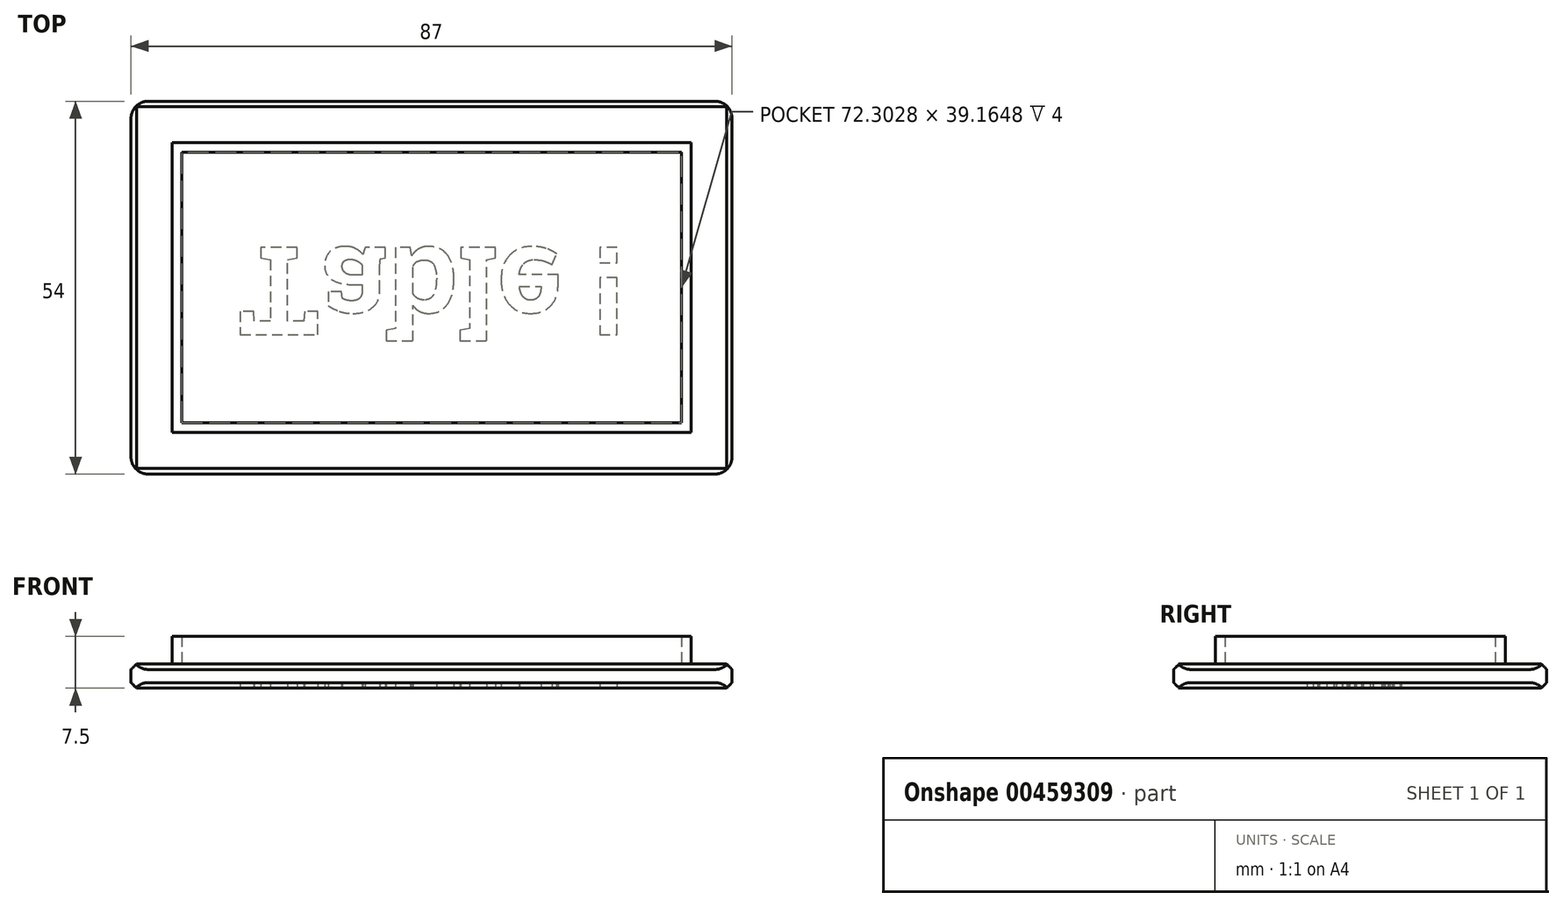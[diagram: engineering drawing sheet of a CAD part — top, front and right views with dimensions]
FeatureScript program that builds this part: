
annotation { "Feature Type Name" : "Feature", "Feature Type Description" : "" }
export const myFeature = defineFeature(function(context is Context, id is Id, definition is map)
    precondition{}
    {
        {
            var Q0;
            Q0=qCreatedBy(makeId("Top.planeOp"),FACE);
            var sketch = newSketch(context, id + "F0", { "sketchPlane" : qUnion([Q0])});
            skLineSegment(sketch, "E0.bottom", {"start": v(43.5, 27) * mm, "end": v(-43.5, 27) * mm});
            skLineSegment(sketch, "E0.top", {"start": v(43.5, -27) * mm, "end": v(-43.5, -27) * mm});
            skLineSegment(sketch, "E0.left", {"start": v(43.5, 27) * mm, "end": v(43.5, -27) * mm});
            skLineSegment(sketch, "E0.right", {"start": v(-43.5, 27) * mm, "end": v(-43.5, -27) * mm});
            skPoint(sketch, "E0.middle", {"position": v(0, 0) * mm});
            skSolve(sketch);
        }
        {
            var Q0;
            Q0 = qSketchRegion(id + "F0", true);
            extrude(context, id + "F1", {"entities" : qUnion([Q0]), "oppositeDirection" : true, "depth" : 3.5 * mm});
        }
        {
            var Q0;
            Q0=makeQuery(id+"F1.opExtrude","CAP_EDGE",EDGE,{"disambiguationData":[OSD([sQuery(id+"F0.wireOp",EDGE,"E0.top")])],"isStart":false});
            var Q1;
            Q1=makeQuery(id+"F1.opExtrude","CAP_EDGE",EDGE,{"disambiguationData":[OSD([sQuery(id+"F0.wireOp",EDGE,"E0.right")])],"isStart":false});
            var Q2;
            Q2=makeQuery(id+"F1.opExtrude","CAP_EDGE",EDGE,{"disambiguationData":[OSD([sQuery(id+"F0.wireOp",EDGE,"E0.bottom")])],"isStart":false});
            var Q3;
            Q3=makeQuery(id+"F1.opExtrude","CAP_EDGE",EDGE,{"disambiguationData":[OSD([sQuery(id+"F0.wireOp",EDGE,"E0.left")])],"isStart":false});
            var Q4;
            Q4=makeQuery(id+"F1.opExtrude","CAP_EDGE",EDGE,{"disambiguationData":[OSD([sQuery(id+"F0.wireOp",EDGE,"E0.top")])],"isStart":true});
            var Q5;
            Q5=makeQuery(id+"F1.opExtrude","CAP_EDGE",EDGE,{"disambiguationData":[OSD([sQuery(id+"F0.wireOp",EDGE,"E0.right")])],"isStart":true});
            var Q6;
            Q6=makeQuery(id+"F1.opExtrude","CAP_EDGE",EDGE,{"disambiguationData":[OSD([sQuery(id+"F0.wireOp",EDGE,"E0.left")])],"isStart":true});
            var Q7;
            Q7=makeQuery(id+"F1.opExtrude","CAP_EDGE",EDGE,{"disambiguationData":[OSD([sQuery(id+"F0.wireOp",EDGE,"E0.bottom")])],"isStart":true});
            chamfer(context, id + "F2", {"entities" : qUnion([Q0, Q1, Q2, Q3, Q4, Q5, Q6, Q7]), "width" : 0.8 * mm, "tangentPropagation" : true});
        }
        {
            var Q0;
            Q0=makeQuery(id+"F1.opExtrude","SWEPT_EDGE",EDGE,{"disambiguationData":[OSD([sQuery(id+"F0.wireOp",EDGE,"E0.top"),sQuery(id+"F0.wireOp",EDGE,"E0.right")])]});
            var Q1;
            Q1=makeQuery(id+"F1.opExtrude","SWEPT_EDGE",EDGE,{"disambiguationData":[OSD([sQuery(id+"F0.wireOp",EDGE,"E0.bottom"),sQuery(id+"F0.wireOp",EDGE,"E0.right")])]});
            var Q2;
            Q2=makeQuery(id+"F1.opExtrude","SWEPT_EDGE",EDGE,{"disambiguationData":[OSD([sQuery(id+"F0.wireOp",EDGE,"E0.bottom"),sQuery(id+"F0.wireOp",EDGE,"E0.left")])]});
            var Q3;
            Q3=makeQuery(id+"F1.opExtrude","SWEPT_EDGE",EDGE,{"disambiguationData":[OSD([sQuery(id+"F0.wireOp",EDGE,"E0.top"),sQuery(id+"F0.wireOp",EDGE,"E0.left")])]});
            fillet(context, id + "F3", {"entities" : qUnion([Q0, Q1, Q2, Q3]), "radius" : 2.5 * mm, "tangentPropagation" : true, "allowEdgeOverflow" : false});
        }
        {
            var Q0;
            Q0=makeQuery(id+"F0.imprint","IMPRINT",FACE,{"disambiguationData":[TD([[makeQuery(id+"F0.imprint","IMPRINT",EDGE,{"derivedFrom":sQuery(id+"F0.wireOp",EDGE,"E0.bottom")}),1.0]])]});
            var sketch = newSketch(context, id + "F4", { "sketchPlane" : qUnion([Q0])});
            skLineSegment(sketch, "E1.bottom", {"start": v(37.55, 20.98) * mm, "end": v(-37.55, 20.98) * mm});
            skLineSegment(sketch, "E1.top", {"start": v(37.55, -20.98) * mm, "end": v(-37.55, -20.98) * mm});
            skLineSegment(sketch, "E1.left", {"start": v(37.55, 20.98) * mm, "end": v(37.55, -20.98) * mm});
            skLineSegment(sketch, "E1.right", {"start": v(-37.55, 20.98) * mm, "end": v(-37.55, -20.98) * mm});
            skPoint(sketch, "E1.middle", {"position": v(0, 0) * mm});
            skLineSegment(sketch, "E2.0", {"start": v(36.15, -19.58) * mm, "end": v(-36.15, -19.58) * mm});
            skLineSegment(sketch, "E2.1", {"start": v(36.15, 19.58) * mm, "end": v(36.15, -19.58) * mm});
            skLineSegment(sketch, "E2.2", {"start": v(36.15, 19.58) * mm, "end": v(-36.15, 19.58) * mm});
            skLineSegment(sketch, "E2.3", {"start": v(-36.15, 19.58) * mm, "end": v(-36.15, -19.58) * mm});
            skSolve(sketch);
        }
        {
            var Q0;
            Q0 = qSketchRegion(id + "F4", true);
            extrude(context, id + "F5", {"entities" : qUnion([Q0]), "operationType" : NewBodyOperationType.ADD, "depth" : 4 * mm});
        }
        {
            var Q0;
            Q0=makeQuery(id+"F4.imprint","IMPRINT",FACE,{"disambiguationData":[TD([[makeQuery(id+"F4.imprint","IMPRINT",EDGE,{"derivedFrom":sQuery(id+"F4.wireOp",EDGE,"E1.bottom")}),-1.0]])]});
            var sketch = newSketch(context, id + "F6", { "sketchPlane" : qUnion([Q0])});
            skCircle(sketch, "E3", {"center": v(-36.85, 20.28) * mm, "radius": 2.2 * mm});
            skLineSegment(sketch, "E4", {"start": v(37.55, 20.98) * mm, "end": v(36.15, 19.58) * mm});
            skLineSegment(sketch, "E5", {"start": v(36.15, -19.58) * mm, "end": v(37.55, -20.98) * mm});
            skLineSegment(sketch, "E6", {"start": v(-36.15, -19.58) * mm, "end": v(-37.55, -20.98) * mm});
            skCircle(sketch, "E7.0.1.0", {"center": v(-36.85, -20.28) * mm, "radius": 2.2 * mm});
            skCircle(sketch, "E7.1.0.0", {"center": v(36.85, 20.28) * mm, "radius": 2.2 * mm});
            skCircle(sketch, "E7.1.1.0", {"center": v(36.85, -20.28) * mm, "radius": 2.2 * mm});
            skLineSegment(sketch, "E7.direction1", {"start": v(-36.85, 20.28) * mm, "end": v(36.85, 20.28) * mm, "construction": true});
            skLineSegment(sketch, "E7.direction2", {"start": v(-36.85, 20.28) * mm, "end": v(-36.85, -20.28) * mm, "construction": true});
            skSolve(sketch);
        }
        {
            var Q0;
            Q0=sQuery(id+"F6.wireOp",EDGE,"E3");
            var Q1;
            Q1=sQuery(id+"F6.wireOp",EDGE,"E7.0.1.0");
            var Q2;
            Q2=sQuery(id+"F6.wireOp",EDGE,"E7.1.1.0");
            var Q3;
            Q3=sQuery(id+"F6.wireOp",EDGE,"E7.1.0.0");
            extrude(context, id + "F7", {"bodyType" : ToolBodyType.SURFACE, "surfaceEntities" : qUnion([Q0, Q1, Q2, Q3]), "depth" : 38 * mm});
        }
        {
            var Q0;
            Q0=makeQuery(id+"F1.opExtrude","CAP_FACE",FACE,{"disambiguationData":[OSD([sQuery(id+"F0.wireOp",EDGE,"E0.bottom"),sQuery(id+"F0.wireOp",EDGE,"E0.top"),sQuery(id+"F0.wireOp",EDGE,"E0.left"),sQuery(id+"F0.wireOp",EDGE,"E0.right")])],"isStart":false});
            var sketch = newSketch(context, id + "F8", { "sketchPlane" : qUnion([Q0])});
            skText(sketch, "E8", { "text": "Table !", "fontName": "RobotoSlab-Bold.ttf"});
            const initialGuessF8  = {"E8": [-0.02804, -0.0058, 1, 0, 0.01277]};
            skSetInitialGuess(sketch, initialGuessF8);
            skSolve(sketch);
        }
        {
            var Q0;
            Q0 = qSketchRegion(id + "F8", true);
            extrude(context, id + "F9", {"entities" : qUnion([Q0]), "operationType" : NewBodyOperationType.REMOVE, "oppositeDirection" : true, "depth" : 0.8 * mm});
        }
    });
